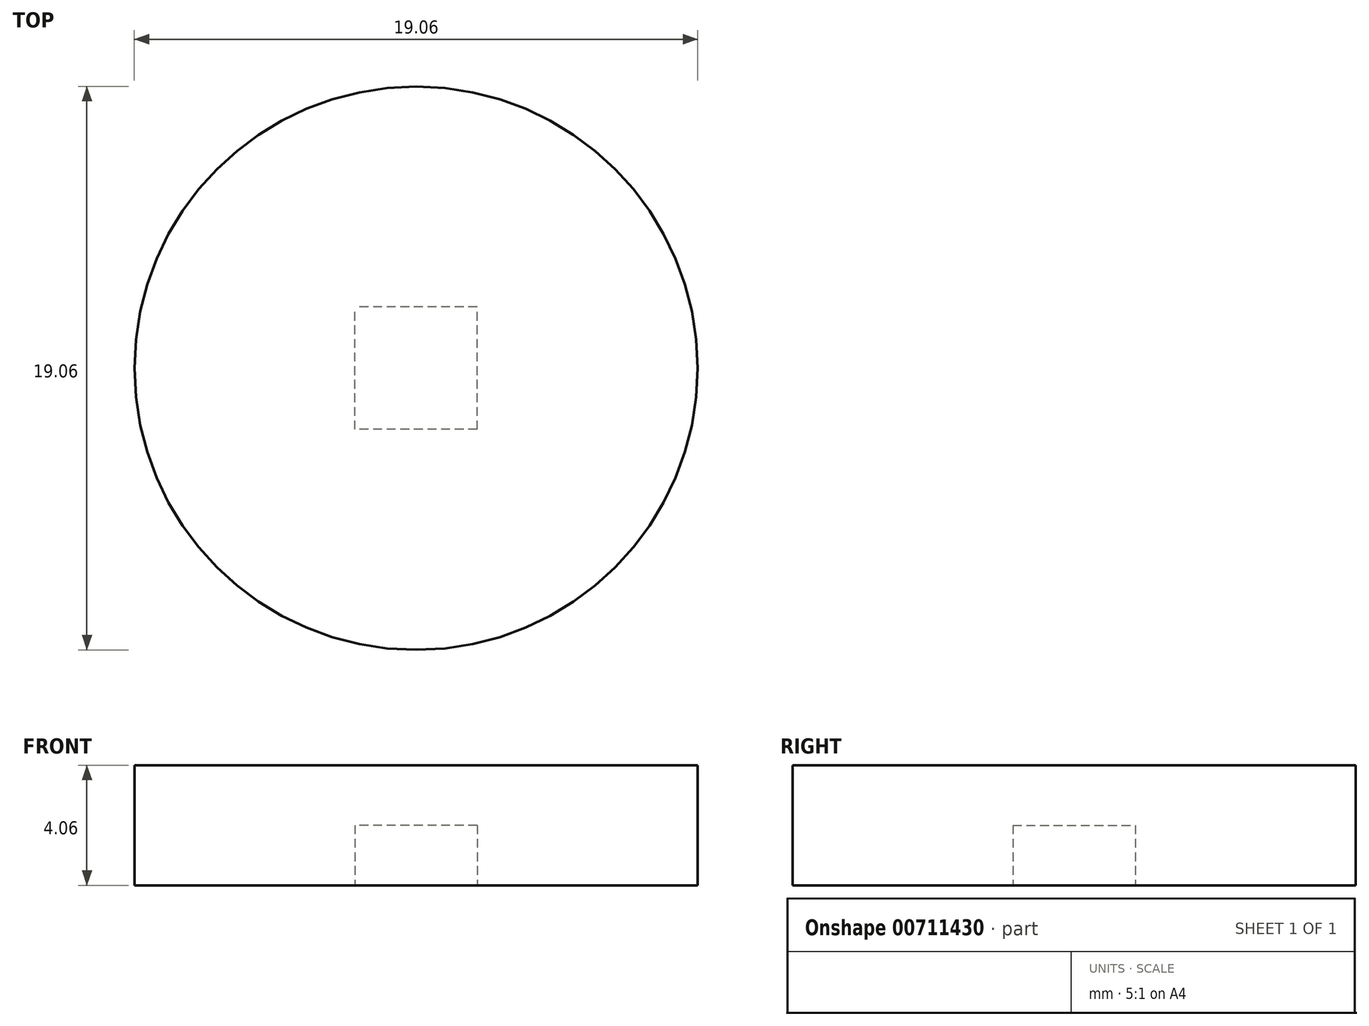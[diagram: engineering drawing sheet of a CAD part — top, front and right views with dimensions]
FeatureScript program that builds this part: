
annotation { "Feature Type Name" : "Feature", "Feature Type Description" : "" }
export const myFeature = defineFeature(function(context is Context, id is Id, definition is map)
    precondition{}
    {
        {
            var Q0;
            Q0=qCreatedBy(makeId("Top.planeOp"),FACE);
            var sketch = newSketch(context, id + "F0", { "sketchPlane" : qUnion([Q0])});
            skCircle(sketch, "E0", {"center": v(0, 0) * mm, "radius": 9.53 * mm});
            skLineSegment(sketch, "E1.bottom", {"start": v(2.07, -2.07) * mm, "end": v(-2.07, -2.07) * mm});
            skLineSegment(sketch, "E1.top", {"start": v(2.07, 2.07) * mm, "end": v(-2.07, 2.07) * mm});
            skLineSegment(sketch, "E1.left", {"start": v(2.07, -2.07) * mm, "end": v(2.07, 2.07) * mm});
            skLineSegment(sketch, "E1.right", {"start": v(-2.07, -2.07) * mm, "end": v(-2.07, 2.07) * mm});
            skSolve(sketch);
        }
        {
            var Q0;
            Q0=makeQuery(id+"F0.imprint","IMPRINT",FACE,{"disambiguationData":[TD([[makeQuery(id+"F0.imprint","IMPRINT",EDGE,{"derivedFrom":sQuery(id+"F0.wireOp",EDGE,"E0")}),1.0]])]});
            var Q1;
            Q1=makeQuery(id+"F0.imprint","IMPRINT",FACE,{"disambiguationData":[TD([[makeQuery(id+"F0.imprint","IMPRINT",EDGE,{"derivedFrom":sQuery(id+"F0.wireOp",EDGE,"E1.bottom")}),-1.0]])]});
            extrude(context, id + "F1", {"entities" : qUnion([Q0, Q1]), "depth" : 4.06 * mm, "offsetDistance" : 25.4 * mm});
        }
        {
            var Q0;
            Q0=makeQuery(id+"F0.imprint","IMPRINT",FACE,{"disambiguationData":[TD([[makeQuery(id+"F0.imprint","IMPRINT",EDGE,{"derivedFrom":sQuery(id+"F0.wireOp",EDGE,"E1.bottom")}),-1.0]])]});
            extrude(context, id + "F2", {"entities" : qUnion([Q0]), "operationType" : NewBodyOperationType.REMOVE, "depth" : 2.03 * mm, "offsetDistance" : 25.4 * mm});
        }
    });
